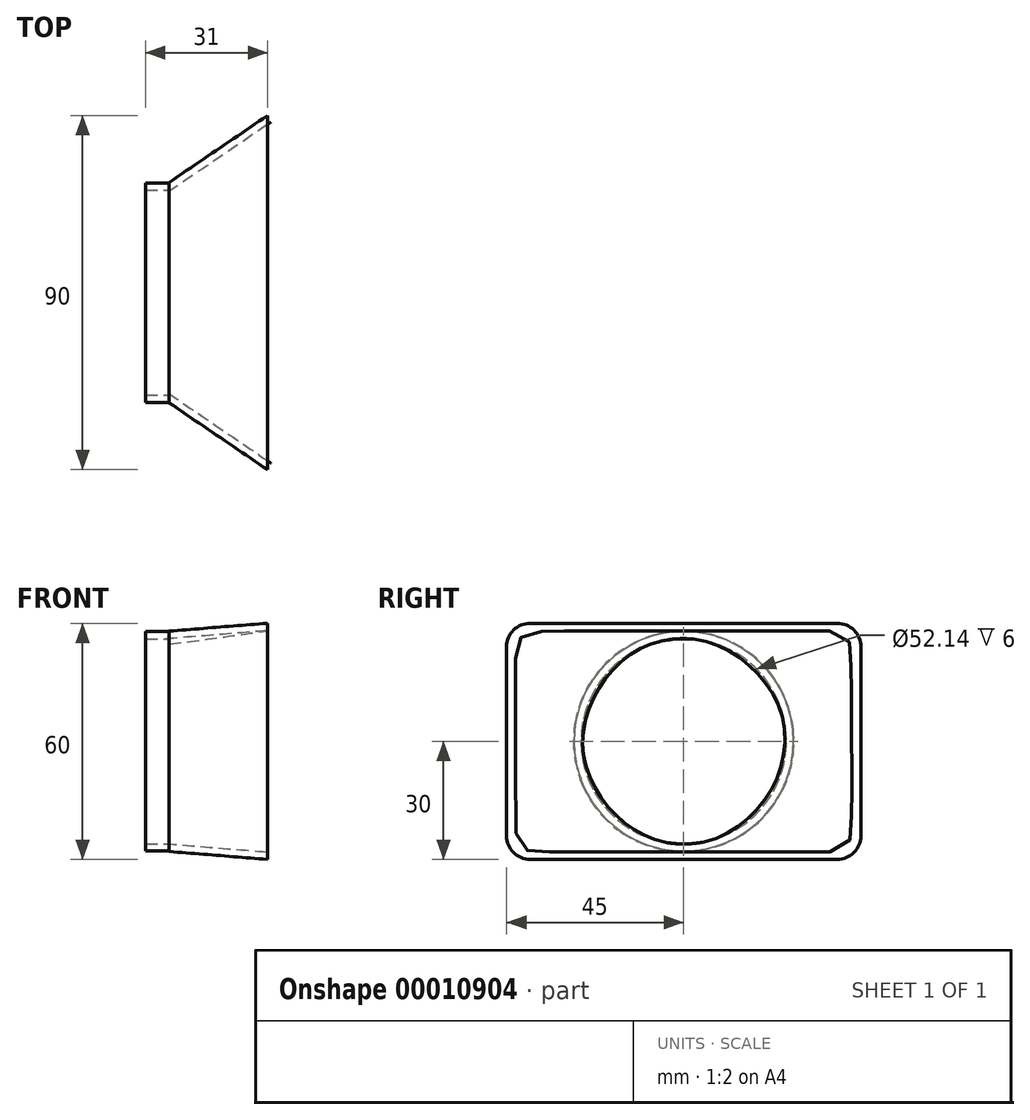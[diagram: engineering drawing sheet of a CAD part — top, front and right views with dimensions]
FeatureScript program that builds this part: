
annotation { "Feature Type Name" : "Feature", "Feature Type Description" : "" }
export const myFeature = defineFeature(function(context is Context, id is Id, definition is map)
    precondition{}
    {
        {
            var Q0;
            Q0=qCreatedBy(makeId("Right.planeOp"),FACE);
            var sketch = newSketch(context, id + "F0", { "sketchPlane" : qUnion([Q0])});
            skCircle(sketch, "E0", {"center": v(0, 0) * mm, "radius": 28 * mm});
            skSolve(sketch);
        }
        {
            var Q0;
            Q0=qCreatedBy(makeId("Right.planeOp"),FACE);
            cPlane(context, id + "F1", {"entities" : qUnion([Q0]), "cplaneType" : CPlaneType.OFFSET, "offset" : 25 * mm, "width" : 150 * mm, "height" : 150 * mm});
        }
        {
            var Q0;
            Q0=qCreatedBy(id+"F1.planeOp",FACE);
            var sketch = newSketch(context, id + "F2", { "sketchPlane" : qUnion([Q0])});
            skLineSegment(sketch, "E1.0", {"start": v(-7.5, 30) * mm, "end": v(-39, 30) * mm});
            skLineSegment(sketch, "E2.0", {"start": v(-7.5, 30) * mm, "end": v(39, 30) * mm});
            skLineSegment(sketch, "E3.0.MirrorCS", {"start": v(-7.5, -30) * mm, "end": v(-39, -30) * mm});
            skLineSegment(sketch, "E4.0.MirrorCS", {"start": v(-7.5, -30) * mm, "end": v(39, -30) * mm});
            skLineSegment(sketch, "E5.0", {"start": v(-45, -24) * mm, "end": v(-45, 24) * mm});
            skLineSegment(sketch, "E6.0", {"start": v(45, -10) * mm, "end": v(45, 24) * mm});
            skLineSegment(sketch, "E7.0", {"start": v(45, -10) * mm, "end": v(45, -24) * mm});
            skPoint(sketch, "E8.0.end.orphan", {"position": v(-35, 25) * mm});
            skPoint(sketch, "E9.0.MirrorCS.end.orphan", {"position": v(-35, -25) * mm});
            skPoint(sketch, "E10.0.MirrorCS.end.orphan", {"position": v(40, -30) * mm});
            skPoint(sketch, "E11.0.MirrorCS.end.orphan", {"position": v(47.5, 35) * mm});
            skPoint(sketch, "E12.orphan", {"position": v(-32.5, 30) * mm});
            skPoint(sketch, "E13.orphan", {"position": v(-7.5, 30) * mm});
            skPoint(sketch, "E14.orphan", {"position": v(17.5, 30) * mm});
            skPoint(sketch, "E15.orphan", {"position": v(-32.5, -30) * mm});
            skPoint(sketch, "E16.orphan", {"position": v(17.5, -30) * mm});
            skLineSegment(sketch, "E17", {"start": v(0, 0) * mm, "end": v(0, 22.47) * mm});
            skLineSegment(sketch, "E18", {"start": v(0, 0) * mm, "end": v(24.53, 0) * mm});
            skPoint(sketch, "E19.visualSharp", {"position": v(-45, 30) * mm});
            skArc(sketch, "E19.filletArc", {"start": v(-39, 30) * mm, "mid": v(-43.24, 28.24) * mm, "end": v(-45, 24) * mm});
            skPoint(sketch, "E20.visualSharp", {"position": v(-45, -30) * mm});
            skArc(sketch, "E20.filletArc", {"start": v(-45, -24) * mm, "mid": v(-43.24, -28.24) * mm, "end": v(-39, -30) * mm});
            skPoint(sketch, "E21.visualSharp", {"position": v(45, -30) * mm});
            skArc(sketch, "E21.filletArc", {"start": v(39, -30) * mm, "mid": v(43.24, -28.24) * mm, "end": v(45, -24) * mm});
            skPoint(sketch, "E22.visualSharp", {"position": v(45, 30) * mm});
            skArc(sketch, "E22.filletArc", {"start": v(45, 24) * mm, "mid": v(43.24, 28.24) * mm, "end": v(39, 30) * mm});
            skSolve(sketch);
        }
        {
            var Q0;
            Q0=makeQuery(id+"F0.imprint","IMPRINT",FACE,{"disambiguationData":[TD([[makeQuery(id+"F0.imprint","IMPRINT",EDGE,{"derivedFrom":sQuery(id+"F0.wireOp",EDGE,"E0")}),1.0]])]});
            var Q1;
            Q1=makeQuery(id+"F2.imprint","IMPRINT",FACE,{"disambiguationData":[TD([[makeQuery(id+"F2.imprint","IMPRINT",EDGE,{"derivedFrom":sQuery(id+"F2.wireOp",EDGE,"E1.0")}),1.0]])]});
            loft(context, id + "F3", {"sheetProfilesArray" : [{ "sheetProfileEntities" : qUnion([Q0]) }, { "sheetProfileEntities" : qUnion([Q1]) }]});
        }
        {
            var Q0;
            Q0=makeQuery(id+"F3.opLoft","CAP_FACE",FACE,{"disambiguationData":[OSD([makeQuery(id+"F0.imprint","IMPRINT",FACE,{"disambiguationData":[TD([[makeQuery(id+"F0.imprint","IMPRINT",EDGE,{"derivedFrom":sQuery(id+"F0.wireOp",EDGE,"E0")}),1.0]])]})])],"isStart":true});
            var Q1;
            Q1=makeQuery(id+"F3.opLoft","CAP_FACE",FACE,{"disambiguationData":[OSD([makeQuery(id+"F2.imprint","IMPRINT",FACE,{"disambiguationData":[TD([[makeQuery(id+"F2.imprint","IMPRINT",EDGE,{"derivedFrom":sQuery(id+"F2.wireOp",EDGE,"E1.0")}),1.0]])]})])],"isStart":true});
            shell(context, id + "F4", {"entities" : qUnion([Q0, Q1]), "thickness" : 1.9 * mm});
        }
        {
            var Q0;
            Q0=makeQuery(id+"F3.opLoft","CAP_FACE",FACE,{"disambiguationData":[OSD([makeQuery(id+"F0.imprint","IMPRINT",FACE,{"disambiguationData":[TD([[makeQuery(id+"F0.imprint","IMPRINT",EDGE,{"derivedFrom":sQuery(id+"F0.wireOp",EDGE,"E0")}),1.0]])]})])],"isStart":true});
            var sketch = newSketch(context, id + "F5", { "sketchPlane" : qUnion([Q0])});
            skCircle(sketch, "E23", {"center": v(0, 0) * mm, "radius": 27.89 * mm});
            skCircle(sketch, "E24", {"center": v(0, 0) * mm, "radius": 26.07 * mm});
            skSolve(sketch);
        }
        {
            var Q0;
            Q0 = qSketchRegion(id + "F5", true);
            extrude(context, id + "F6", {"entities" : qUnion([Q0]), "operationType" : NewBodyOperationType.ADD, "depth" : 6 * mm});
        }
    });
